# Revit family: Mirror-DXV-Modulus-D19055049.191
name_source: partatom
category: Furniture
units: mm (PartAtom-declared; Revit-internal decimal feet)

## family parameters
Cut with Voids When Loaded = No
Host = Face
OmniClass Number = 23.40.95.17.17
OmniClass Title = Mirrors
Room Calculation Point = No
Shared = Yes

## types (1)
- D19055049.191
    Assembly Code = E2010
    Default Elevation = 35"
    Description = DXV Modulus Mirror - Double
    Finish = Mirror-DXV
    Height = 20 1/16"
    Installation Instruction Link = https://dxv01.blob.core.windows.net
    Installation Type = Wall-Mount
    Length = 1 9/16"
    Manufacturer = DXV
    Material = Mirror-DXV
    Model = D19055049.191
    Price = Prices may vary. Please consult Manufacturer Representative for most up-to-date price list.
    Product Documentation Link = https://dxv01.blob.core.windows.net
    Product Page URL = https://www.dxv.com
    Revised Date = 05/10/2022
    URL = https://www.dxv.com
    Width = 49 3/16"

## geometry (parser evidence)
native form markers: Sweep x3
no freeform markers — native parametric forms only
